# Revit family: PLC_ARR_3S
name_source: partatom
category: Mechanical Equipment
units: mm (PartAtom-declared; Revit-internal decimal feet)

## family parameters
Always vertical = Yes
Cut with Voids When Loaded = No
Part Type = Normal
Room Calculation Point = No
Round Connector Dimension = Use Diameter
Shared = No
Work Plane-Based = No

## types (40) — shared parameters
0 = 0' - 0"
1" = 0' - 1"
1.5 = 0' - 1 1/2"
120 = 90.00°
2" = 0' - 2"
2' = 2' - 0"
25 = 25.00°
3" = 0' - 3"
4" = 0' - 4"
60 = 60.00°
Manufacturer = Loren Cook Company
Model = PLC Arrangement 3S
ONE EIGTH = 0' - 0 1/8"
URL = www.lorencook.com

## per-type parameters (varying)
- 120_PLC_CLASS_1_3S: -(H-.125")=-0' - 1 11/16"; -F=-1' - 1 1/16"; -F/2=-0' - 6 17/32"; -H+.375"=-0' - 1 7/16"; A=1' - 5 1/4"; A/2=0' - 8 5/8"; B=1' - 5 1/4"; B/2=0' - 8 5/8"; C=0' - 8 5/8"; C*.2=0' - 2 19/32"; C*.66=0' - 5 11/16"; C-M=0' - 7 7/16"; C/2=0' - 4 5/16"; D=0' - 8 5/8"; E=0' - 7 11/16"; F=1' - 1 1/16"; F-H-H=0' - 9 7/16"; G=0' - 7 7/16"; H=0' - 1 13/16"; H-.125"=0' - 1 11/16"; J=0' - 2 13/16"; K=1' - 4 15/16"; K-F=0' - 3 7/8"; L=0' - 0 5/8"; L/2=0' - 0 5/16"; M=0' - 1 3/16"; M*2=0' - 2 3/8"; M/2=0' - 0 19/32"; MB/2=0' - 5 1/4"; MH/2=0' - 5 1/4"; MOTOR_BASE=0' - 10 1/2"; MOTOR_HEIGHT=0' - 10 1/2"; N=1' - 4 3/4"; P=0' - 0 5/8"; Type Comments=Centrifugal Plenum Fan Side Mount Arrangement 3S Class 1
- 135_PLC_CLASS_1_3S: -(H-.125")=-0' - 1 15/16"; -F=-1' - 2 5/8"; -F/2=-0' - 7 5/16"; -H+.375"=-0' - 1 11/16"; A=1' - 7 1/2"; A/2=0' - 9 3/4"; B=1' - 7 1/2"; B/2=0' - 9 3/4"; C=0' - 9 3/4"; C*.2=0' - 2 15/16"; C*.66=0' - 6 7/16"; C-M=0' - 8 9/16"; C/2=0' - 4 7/8"; D=0' - 9 3/4"; E=0' - 8 13/16"; F=1' - 2 5/8"; F-H-H=0' - 10 1/2"; G=0' - 8 1/2"; H=0' - 2 1/16"; H-.125"=0' - 1 15/16"; J=0' - 3 1/16"; K=1' - 6 1/2"; K-F=0' - 3 7/8"; L=0' - 0 5/8"; L/2=0' - 0 5/16"; M=0' - 1 3/16"; M*2=0' - 2 3/8"; M/2=0' - 0 19/32"; MB/2=0' - 5 1/4"; MH/2=0' - 5 1/4"; MOTOR_BASE=0' - 10 1/2"; MOTOR_HEIGHT=0' - 10 1/2"; N=1' - 6 5/8"; P=0' - 0 5/8"; Type Comments=Centrifugal Plenum Fan Side Mount Arrangement 3S Class 1
- 150_PLC_CLASS_1_3S: -(H-.125")=-0' - 1 15/16"; -F=-1' - 3 9/16"; -F/2=-0' - 7 25/32"; -H+.375"=-0' - 1 11/16"; A=1' - 9 1/2"; A/2=0' - 10 3/4"; B=1' - 9 1/2"; B/2=0' - 10 3/4"; C=0' - 10 3/4"; C*.2=0' - 3 7/32"; C*.66=0' - 7 3/32"; C-M=0' - 9 9/16"; C/2=0' - 5 3/8"; D=0' - 10 3/4"; E=0' - 9 13/16"; F=1' - 3 9/16"; F-H-H=0' - 11 7/16"; G=0' - 9 7/16"; H=0' - 2 1/16"; H-.125"=0' - 1 15/16"; J=0' - 3 1/16"; K=1' - 7 7/16"; K-F=0' - 3 7/8"; L=0' - 0 5/8"; L/2=0' - 0 5/16"; M=0' - 1 3/16"; M*2=0' - 2 3/8"; M/2=0' - 0 19/32"; MB/2=0' - 5 1/4"; MH/2=0' - 5 1/4"; MOTOR_BASE=0' - 10 1/2"; MOTOR_HEIGHT=0' - 10 1/2"; N=1' - 8 1/8"; P=0' - 0 5/8"; Type Comments=Centrifugal Plenum Fan Side Mount Arrangement 3S Class 1
- 165_PLC_CLASS_1_3S: -(H-.125")=-0' - 1 15/16"; -F=-1' - 4 3/4"; -F/2=-0' - 8 3/8"; -H+.375"=-0' - 1 11/16"; A=1' - 11 3/4"; A/2=0' - 11 7/8"; B=1' - 11 3/4"; B/2=0' - 11 7/8"; C=0' - 11 7/8"; C*.2=0' - 3 9/16"; C*.66=0' - 7 27/32"; C-M=0' - 10 11/16"; C/2=0' - 5 15/16"; D=0' - 11 7/8"; E=0' - 10 15/16"; F=1' - 4 3/4"; F-H-H=1' - 0 5/8"; G=0' - 10 5/8"; H=0' - 2 1/16"; H-.125"=0' - 1 15/16"; J=0' - 3 1/16"; K=1' - 8 5/8"; K-F=0' - 3 7/8"; L=0' - 0 5/8"; L/2=0' - 0 5/16"; M=0' - 1 3/16"; M*2=0' - 2 3/8"; M/2=0' - 0 19/32"; MB/2=0' - 5 1/4"; MH/2=0' - 5 1/4"; MOTOR_BASE=0' - 10 1/2"; MOTOR_HEIGHT=0' - 10 1/2"; N=1' - 9 3/4"; P=0' - 0 5/8"; Type Comments=Centrifugal Plenum Fan Side Mount Arrangement 3S Class 1
- 180_PLC_CLASS_1_3S: -(H-.125")=-0' - 2 15/16"; -F=-1' - 7 7/8"; -F/2=-0' - 9 15/16"; -H+.375"=-0' - 2 11/16"; A=2' - 1 3/4"; A/2=1' - 0 7/8"; B=2' - 1 3/4"; B/2=1' - 0 7/8"; C=1' - 0 7/8"; C*.2=0' - 3 7/8"; C*.66=0' - 8 1/2"; C-M=0' - 11 7/16"; C/2=0' - 6 7/16"; D=1' - 0 7/8"; E=1' - 0"; F=1' - 7 7/8"; F-H-H=1' - 1 3/4"; G=0' - 11 3/4"; H=0' - 3 1/16"; H-.125"=0' - 2 15/16"; J=0' - 4 1/16"; K=2' - 0"; K-F=0' - 4 1/8"; L=0' - 0 5/8"; L/2=0' - 0 5/16"; M=0' - 1 7/16"; M*2=0' - 2 7/8"; M/2=0' - 0 23/32"; MB/2=0' - 5 1/4"; MH/2=0' - 5 1/4"; MOTOR_BASE=0' - 10 1/2"; MOTOR_HEIGHT=0' - 10 1/2"; N=1' - 11 1/4"; P=0' - 0 5/8"; Type Comments=Centrifugal Plenum Fan Side Mount Arrangement 3S Class 1
- 195_PLC_CLASS_1_3S: -(H-.125")=-0' - 2 15/16"; -F=-1' - 9"; -F/2=-0' - 10 1/2"; -H+.375"=-0' - 2 11/16"; A=2' - 4"; A/2=1' - 2"; B=2' - 4"; B/2=1' - 2"; C=1' - 2"; C*.2=0' - 4 3/16"; C*.66=0' - 9 1/4"; C-M=1' - 0 9/16"; C/2=0' - 7"; D=1' - 2"; E=1' - 1 1/8"; F=1' - 9"; F-H-H=1' - 2 7/8"; G=1' - 0 7/8"; H=0' - 3 1/16"; H-.125"=0' - 2 15/16"; J=0' - 4 1/16"; K=2' - 1 1/8"; K-F=0' - 4 1/8"; L=0' - 0 5/8"; L/2=0' - 0 5/16"; M=0' - 1 7/16"; M*2=0' - 2 7/8"; M/2=0' - 0 23/32"; MB/2=0' - 6 5/16"; MH/2=0' - 6 5/16"; MOTOR_BASE=1' - 0 5/8"; MOTOR_HEIGHT=1' - 0 5/8"; N=2' - 1"; P=0' - 0 5/8"; Type Comments=Centrifugal Plenum Fan Side Mount Arrangement 3S Class 1
- 210_PLC_CLASS_1_3S: -(H-.125")=-0' - 2 15/16"; -F=-1' - 10 1/16"; -F/2=-0' - 11 1/32"; -H+.375"=-0' - 2 11/16"; A=2' - 6"; A/2=1' - 3"; B=2' - 6"; B/2=1' - 3"; C=1' - 3"; C*.2=0' - 4 1/2"; C*.66=0' - 9 29/32"; C-M=1' - 1 9/16"; C/2=0' - 7 1/2"; D=1' - 3"; E=1' - 2 1/8"; F=1' - 10 1/16"; F-H-H=1' - 3 15/16"; G=1' - 1 15/16"; H=0' - 3 1/16"; H-.125"=0' - 2 15/16"; J=0' - 4 1/16"; K=2' - 2 3/16"; K-F=0' - 4 1/8"; L=0' - 0 5/8"; L/2=0' - 0 5/16"; M=0' - 1 7/16"; M*2=0' - 2 7/8"; M/2=0' - 0 23/32"; MB/2=0' - 6 5/16"; MH/2=0' - 6 5/16"; MOTOR_BASE=1' - 0 5/8"; MOTOR_HEIGHT=1' - 0 5/8"; N=2' - 2 1/2"; P=0' - 1"; Type Comments=Centrifugal Plenum Fan Side Mount Arrangement 3S Class 1
- 225_PLC_CLASS_1_3S: -(H-.125")=-0' - 2 15/16"; -F=-1' - 11 1/16"; -F/2=-0' - 11 17/32"; -H+.375"=-0' - 2 11/16"; A=2' - 8 1/4"; A/2=1' - 4 1/8"; B=2' - 8 1/4"; B/2=1' - 4 1/8"; C=1' - 4 1/8"; C*.2=0' - 4 27/32"; C*.66=0' - 10 21/32"; C-M=1' - 2 11/16"; C/2=0' - 8 1/16"; D=1' - 4 1/8"; E=1' - 3 5/16"; F=1' - 11 1/16"; F-H-H=1' - 4 15/16"; G=1' - 2 15/16"; H=0' - 3 1/16"; H-.125"=0' - 2 15/16"; J=0' - 4 1/16"; K=2' - 3 3/16"; K-F=0' - 4 1/8"; L=0' - 0 5/8"; L/2=0' - 0 5/16"; M=0' - 1 7/16"; M*2=0' - 2 7/8"; M/2=0' - 0 23/32"; MB/2=0' - 6 5/16"; MH/2=0' - 6 5/16"; MOTOR_BASE=1' - 0 5/8"; MOTOR_HEIGHT=1' - 0 5/8"; N=2' - 4 1/8"; P=0' - 1"; Type Comments=Centrifugal Plenum Fan Side Mount Arrangement 3S Class 1
- 245_PLC_CLASS_1_3S: -(H-.125")=-0' - 2 15/16"; -F=-2' - 0 1/2"; -F/2=-1' - 0 1/4"; -H+.375"=-0' - 2 11/16"; A=2' - 11"; A/2=1' - 5 1/2"; B=2' - 11"; B/2=1' - 5 1/2"; C=1' - 5 1/2"; C*.2=0' - 5 1/4"; C*.66=0' - 11 9/16"; C-M=1' - 4 1/16"; C/2=0' - 8 3/4"; D=1' - 5 1/2"; E=1' - 4 7/16"; F=2' - 0 1/2"; F-H-H=1' - 6 3/8"; G=1' - 3 7/8"; H=0' - 3 1/16"; H-.125"=0' - 2 15/16"; J=0' - 4 5/16"; K=2' - 4 3/4"; K-F=0' - 4 1/4"; L=0' - 0 5/8"; L/2=0' - 0 5/16"; M=0' - 1 7/16"; M*2=0' - 2 7/8"; M/2=0' - 0 23/32"; MB/2=0' - 6 5/16"; MH/2=0' - 6 5/16"; MOTOR_BASE=1' - 0 5/8"; MOTOR_HEIGHT=1' - 0 5/8"; N=2' - 6 1/8"; P=0' - 1"; Type Comments=Centrifugal Plenum Fan Side Mount Arrangement 3S Class 1
- 270_PLC_CLASS_1_3S: -(H-.125")=-0' - 3 7/16"; -F=-2' - 3 7/16"; -F/2=-1' - 1 23/32"; -H+.375"=-0' - 3 3/16"; A=3' - 2 3/4"; A/2=1' - 7 3/8"; B=3' - 2 3/4"; B/2=1' - 7 3/8"; C=1' - 7 3/8"; C*.2=0' - 5 13/16"; C*.66=1' - 0 25/32"; C-M=1' - 5 15/16"; C/2=0' - 9 11/16"; D=1' - 7 3/8"; E=1' - 6 5/16"; F=2' - 3 7/16"; F-H-H=1' - 8 5/16"; G=1' - 5 13/16"; H=0' - 3 9/16"; H-.125"=0' - 3 7/16"; J=0' - 4 13/16"; K=2' - 7 11/16"; K-F=0' - 4 1/4"; L=0' - 0 5/8"; L/2=0' - 0 5/16"; M=0' - 1 7/16"; M*2=0' - 2 7/8"; M/2=0' - 0 23/32"; MB/2=0' - 7"; MH/2=0' - 7"; MOTOR_BASE=1' - 2"; MOTOR_HEIGHT=1' - 2"; N=2' - 10 1/2"; P=0' - 1"; Type Comments=Centrifugal Plenum Fan Side Mount Arrangement 3S Class 1
- 300_PLC_CLASS_1_3S: -(H-.125")=-0' - 3 7/16"; -F=-2' - 5 1/2"; -F/2=-1' - 2 3/4"; -H+.375"=-0' - 3 3/16"; A=3' - 7"; A/2=1' - 9 1/2"; B=3' - 7"; B/2=1' - 9 1/2"; C=1' - 9 1/2"; C*.2=0' - 6 7/16"; C*.66=1' - 2 3/16"; C-M=1' - 7 13/16"; C/2=0' - 10 3/4"; D=1' - 9 1/2"; E=1' - 8 3/16"; F=2' - 5 1/2"; F-H-H=1' - 10 3/8"; G=1' - 7 3/8"; H=0' - 3 9/16"; H-.125"=0' - 3 7/16"; J=0' - 5 1/16"; K=2' - 9 7/8"; K-F=0' - 4 3/8"; L=0' - 0 5/8"; L/2=0' - 0 5/16"; M=0' - 1 11/16"; M*2=0' - 3 3/8"; M/2=0' - 0 27/32"; MB/2=0' - 7"; MH/2=0' - 7"; MOTOR_BASE=1' - 2"; MOTOR_HEIGHT=1' - 2"; N=2' - 11 5/8"; P=0' - 1"; Type Comments=Centrifugal Plenum Fan Side Mount Arrangement 3S Class 1
- 330_PLC_CLASS_1_3S: -(H-.125")=-0' - 3 7/16"; -F=-2' - 8 3/16"; -F/2=-1' - 4 3/32"; -H+.375"=-0' - 3 3/16"; A=4' - 1 1/2"; A/2=2' - 0 3/4"; B=3' - 10"; B/2=1' - 11"; C=1' - 11 5/8"; C*.2=0' - 7 3/32"; C*.66=1' - 3 19/32"; C-M=1' - 9 11/16"; C/2=0' - 11 13/16"; D=1' - 11"; E=1' - 10 5/16"; F=2' - 8 3/16"; F-H-H=2' - 1 1/16"; G=2' - 2 3/8"; H=0' - 3 9/16"; H-.125"=0' - 3 7/16"; J=0' - 4 11/16"; K=3' - 0 13/16"; K-F=0' - 4 5/8"; L=0' - 0 15/16"; L/2=0' - 0 15/32"; M=0' - 1 15/16"; M*2=0' - 3 7/8"; M/2=0' - 0 31/32"; MB/2=0' - 6 5/16"; MH/2=0' - 6 5/16"; MOTOR_BASE=1' - 0 5/8"; MOTOR_HEIGHT=1' - 0 5/8"; N=3' - 1 5/8"; P=0' - 1"; Type Comments=Centrifugal Plenum Fan Side Mount Arrangement 3S Class 1
- 365_PLC_CLASS_1_3S: -(H-.125")=-0' - 3 7/16"; -F=-2' - 10 9/16"; -F/2=-1' - 5 9/32"; -H+.375"=-0' - 3 3/16"; A=4' - 5 1/2"; A/2=2' - 2 3/4"; B=4' - 1"; B/2=2' - 0 1/2"; C=2' - 2 1/8"; C*.2=0' - 7 27/32"; C*.66=1' - 5 1/4"; C-M=2' - 0 3/16"; C/2=1' - 1 1/16"; D=2' - 0 1/2"; E=1' - 11 13/16"; F=2' - 10 9/16"; F-H-H=2' - 3 7/16"; G=2' - 4 3/4"; H=0' - 3 9/16"; H-.125"=0' - 3 7/16"; J=0' - 4 11/16"; K=3' - 3 5/16"; K-F=0' - 4 3/4"; L=0' - 0 15/16"; L/2=0' - 0 15/32"; M=0' - 1 15/16"; M*2=0' - 3 7/8"; M/2=0' - 0 31/32"; MB/2=0' - 6 5/16"; MH/2=0' - 6 5/16"; MOTOR_BASE=1' - 0 5/8"; MOTOR_HEIGHT=1' - 0 5/8"; N=3' - 4"; P=0' - 1"; Type Comments=Centrifugal Plenum Fan Side Mount Arrangement 3S Class 1
- 402_PLC_CLASS_1_3S: -(H-.125")=-0' - 4 7/16"; -F=-3' - 3 7/16"; -F/2=-1' - 7 23/32"; -H+.375"=-0' - 4 3/16"; A=5' - 0"; A/2=2' - 6"; B=4' - 6"; B/2=2' - 3"; C=2' - 4 3/4"; C*.2=0' - 8 5/8"; C*.66=1' - 6 31/32"; C-M=2' - 2 5/16"; C/2=1' - 2 3/8"; D=2' - 3"; E=2' - 2 1/4"; F=3' - 3 7/16"; F-H-H=2' - 6 5/16"; G=2' - 8 5/8"; H=0' - 4 9/16"; H-.125"=0' - 4 7/16"; J=0' - 5 11/16"; K=3' - 8 7/16"; K-F=0' - 5"; L=0' - 0 15/16"; L/2=0' - 0 15/32"; M=0' - 2 7/16"; M*2=0' - 4 7/8"; M/2=0' - 1 7/32"; MB/2=0' - 7"; MH/2=0' - 7"; MOTOR_BASE=1' - 2"; MOTOR_HEIGHT=1' - 2"; N=3' - 7 7/8"; P=0' - 1"; Type Comments=Centrifugal Plenum Fan Side Mount Arrangement 3S Class 1
- 445_PLC_CLASS_1_3S: -(H-.125")=-0' - 4 15/16"; -F=-3' - 7"; -F/2=-1' - 9 1/2"; -H+.375"=-0' - 4 11/16"; A=5' - 4"; A/2=2' - 8"; B=4' - 10 1/2"; B/2=2' - 5 1/4"; C=2' - 7 7/8"; C*.2=0' - 9 9/16"; C*.66=1' - 9 1/32"; C-M=2' - 5 7/16"; C/2=1' - 3 15/16"; D=2' - 5 1/4"; E=2' - 4 1/2"; F=3' - 7"; F-H-H=2' - 8 7/8"; G=2' - 11 5/8"; H=0' - 5 1/16"; H-.125"=0' - 4 15/16"; J=0' - 6 1/4"; K=4' - 0 1/8"; K-F=0' - 5 1/8"; L=0' - 0 15/16"; L/2=0' - 0 15/32"; M=0' - 2 7/16"; M*2=0' - 4 7/8"; M/2=0' - 1 7/32"; MB/2=0' - 8"; MH/2=0' - 8"; MOTOR_BASE=1' - 4"; MOTOR_HEIGHT=1' - 4"; N=3' - 11 1/8"; P=0' - 1"; Type Comments=Centrifugal Plenum Fan Side Mount Arrangement 3S Class 1
- 490_PLC_CLASS_1_3S: -(H-.125")=-0' - 4 15/16"; -F=-3' - 11 1/4"; -F/2=-1' - 11 5/8"; -H+.375"=-0' - 4 11/16"; A=5' - 10"; A/2=2' - 11"; B=5' - 3"; B/2=2' - 7 1/2"; C=2' - 11"; C*.2=0' - 10 1/2"; C*.66=1' - 11 3/32"; C-M=2' - 8 9/16"; C/2=1' - 5 1/2"; D=2' - 7 1/2"; E=2' - 6 5/8"; F=3' - 11 1/4"; F-H-H=3' - 1 1/8"; G=3' - 3 7/8"; H=0' - 5 1/16"; H-.125"=0' - 4 15/16"; J=0' - 6 1/4"; K=4' - 4 5/8"; K-F=0' - 5 3/8"; L=0' - 0 15/16"; L/2=0' - 0 15/32"; M=0' - 2 7/16"; M*2=0' - 4 7/8"; M/2=0' - 1 7/32"; MB/2=0' - 8"; MH/2=0' - 8"; MOTOR_BASE=1' - 4"; MOTOR_HEIGHT=1' - 4"; N=4' - 2 3/8"; P=0' - 1"; Type Comments=Centrifugal Plenum Fan Side Mount Arrangement 3S Class 1
- 540_PLC_CLASS_1_3S: -(H-.125")=-0' - 5"; -F=-4' - 2 7/8"; -F/2=-2' - 1 7/16"; -H+.375"=-0' - 4 3/4"; A=6' - 3"; A/2=3' - 1 1/2"; B=5' - 9"; B/2=2' - 10 1/2"; C=3' - 2 5/8"; C*.2=0' - 11 19/32"; C*.66=2' - 1 1/2"; C-M=3' - 0 3/16"; C/2=1' - 7 5/16"; D=2' - 10 1/2"; E=2' - 9 5/8"; F=4' - 2 7/8"; F-H-H=3' - 4 5/8"; G=3' - 7 1/2"; H=0' - 5 1/8"; H-.125"=0' - 5"; J=0' - 6 1/4"; K=4' - 8 1/2"; K-F=0' - 5 5/8"; L=0' - 1 1/16"; L/2=0' - 0 17/32"; M=0' - 2 7/16"; M*2=0' - 4 7/8"; M/2=0' - 1 7/32"; MB/2=0' - 8"; MH/2=0' - 8"; MOTOR_BASE=1' - 4"; MOTOR_HEIGHT=1' - 4"; N=4' - 6 1/4"; P=0' - 1 1/4"; Type Comments=Centrifugal Plenum Fan Side Mount Arrangement 3S Class 1
- 600_PLC_CLASS_1_3S: -(H-.125")=-0' - 6"; -F=-4' - 10 1/4"; -F/2=-2' - 5 1/8"; -H+.375"=-0' - 5 3/4"; A=6' - 10"; A/2=3' - 5"; B=6' - 3"; B/2=3' - 1 1/2"; C=3' - 6 7/8"; C*.2=1' - 0 7/8"; C*.66=2' - 4 5/16"; C-M=3' - 4 3/16"; C/2=1' - 9 7/16"; D=3' - 1 1/2"; E=3' - 0 5/8"; F=4' - 10 1/4"; F-H-H=3' - 10"; G=3' - 11 7/8"; H=0' - 6 1/8"; H-.125"=0' - 6"; J=0' - 7 1/4"; K=5' - 2 1/4"; K-F=0' - 4"; L=0' - 1 1/16"; L/2=0' - 0 17/32"; M=0' - 2 11/16"; M*2=0' - 5 3/8"; M/2=0' - 1 11/32"; MB/2=0' - 9"; MH/2=0' - 9"; MOTOR_BASE=1' - 6"; MOTOR_HEIGHT=1' - 6"; N=4' - 9 7/8"; P=0' - 1 1/4"; Type Comments=Centrifugal Plenum Fan Side Mount Arrangement 3S Class 1
- 660_PLC_CLASS_1_3S: -(H-.125")=-0' - 7"; -F=-5' - 3 11/16"; -F/2=-2' - 7 27/32"; -H+.375"=-0' - 6 3/4"; A=7' - 6"; A/2=3' - 9"; B=6' - 10"; B/2=3' - 5"; C=3' - 11 1/4"; C*.2=1' - 2 3/16"; C*.66=2' - 7 3/16"; C-M=3' - 8 5/16"; C/2=1' - 11 5/8"; D=3' - 5"; E=3' - 4"; F=5' - 3 11/16"; F-H-H=4' - 1 7/16"; G=4' - 6 5/16"; H=0' - 7 1/8"; H-.125"=0' - 7"; J=0' - 8 1/4"; K=5' - 10 5/16"; K-F=0' - 6 5/8"; L=0' - 1 1/16"; L/2=0' - 0 17/32"; M=0' - 2 15/16"; M*2=0' - 5 7/8"; M/2=0' - 1 15/32"; MB/2=0' - 9"; MH/2=0' - 9"; MOTOR_BASE=1' - 6"; MOTOR_HEIGHT=1' - 6"; N=5' - 2 7/8"; P=0' - 1 1/2"; Type Comments=Centrifugal Plenum Fan Side Mount Arrangement 3S Class 1
- 730_PLC_CLASS_1_3S: -(H-.125")=-0' - 8"; -F=-5' - 9 11/16"; -F/2=-2' - 10 27/32"; -H+.375"=-0' - 7 3/4"; A=7' - 8"; A/2=3' - 10"; B=7' - 8"; B/2=3' - 10"; C=4' - 4 1/4"; C*.2=1' - 3 11/16"; C*.66=2' - 10 1/2"; C-M=4' - 0 13/16"; C/2=2' - 2 1/8"; D=3' - 10"; E=3' - 9"; F=5' - 9 11/16"; F-H-H=4' - 5 7/16"; G=4' - 11 5/16"; H=0' - 8 1/8"; H-.125"=0' - 8"; J=0' - 9 1/4"; K=6' - 4 15/16"; K-F=0' - 7 1/4"; L=0' - 1 1/16"; L/2=0' - 0 17/32"; M=0' - 3 7/16"; M*2=0' - 6 7/8"; M/2=0' - 1 23/32"; MB/2=0' - 11"; MH/2=0' - 11 3/4"; MOTOR_BASE=1' - 10"; MOTOR_HEIGHT=1' - 11 1/2"; N=5' - 8 1/2"; P=0' - 1 1/2"; Type Comments=Centrifugal Plenum Fan Side Mount Arrangement 3S Class 1
- 120_PLC_CLASS_2_3S: -(H-.125")=-0' - 1 11/16"; -F=-1' - 1 1/16"; -F/2=-0' - 6 17/32"; -H+.375"=-0' - 1 7/16"; A=1' - 5 1/4"; A/2=0' - 8 5/8"; B=1' - 5 1/4"; B/2=0' - 8 5/8"; C=0' - 8 5/8"; C*.2=0' - 2 19/32"; C*.66=0' - 5 11/16"; C-M=0' - 7 3/16"; C/2=0' - 4 5/16"; D=0' - 8 5/8"; E=0' - 7 11/16"; F=1' - 1 1/16"; F-H-H=0' - 9 7/16"; G=0' - 7 7/16"; H=0' - 1 13/16"; H-.125"=0' - 1 11/16"; J=0' - 2 13/16"; K=1' - 5 5/16"; K-F=0' - 4 1/4"; L=0' - 0 5/8"; L/2=0' - 0 5/16"; M=0' - 1 7/16"; M*2=0' - 2 7/8"; M/2=0' - 0 23/32"; MB/2=0' - 5 1/4"; MH/2=0' - 5 1/4"; MOTOR_BASE=0' - 10 1/2"; MOTOR_HEIGHT=0' - 10 1/2"; N=1' - 4 3/4"; P=0' - 0 5/8"; Type Comments=Centrifugal Plenum Fan Side Mount Arrangement 3S Class 2
- 135_PLC_CLASS_2_3S: -(H-.125")=-0' - 1 15/16"; -F=-1' - 2 5/8"; -F/2=-0' - 7 5/16"; -H+.375"=-0' - 1 11/16"; A=1' - 7 1/2"; A/2=0' - 9 3/4"; B=1' - 7 1/2"; B/2=0' - 9 3/4"; C=0' - 9 3/4"; C*.2=0' - 2 15/16"; C*.66=0' - 6 7/16"; C-M=0' - 8 5/16"; C/2=0' - 4 7/8"; D=0' - 9 3/4"; E=0' - 8 13/16"; F=1' - 2 5/8"; F-H-H=0' - 10 1/2"; G=0' - 8 1/2"; H=0' - 2 1/16"; H-.125"=0' - 1 15/16"; J=0' - 3 1/16"; K=1' - 6 7/8"; K-F=0' - 4 1/4"; L=0' - 0 5/8"; L/2=0' - 0 5/16"; M=0' - 1 7/16"; M*2=0' - 2 7/8"; M/2=0' - 0 23/32"; MB/2=0' - 5 1/4"; MH/2=0' - 5 1/4"; MOTOR_BASE=0' - 10 1/2"; MOTOR_HEIGHT=0' - 10 1/2"; N=1' - 6 5/8"; P=0' - 0 5/8"; Type Comments=Centrifugal Plenum Fan Side Mount Arrangement 3S Class 2
- 150_PLC_CLASS_2_3S: -(H-.125")=-0' - 1 15/16"; -F=-1' - 3 9/16"; -F/2=-0' - 7 25/32"; -H+.375"=-0' - 1 11/16"; A=1' - 9 1/2"; A/2=0' - 10 3/4"; B=1' - 9 1/2"; B/2=0' - 10 3/4"; C=0' - 10 3/4"; C*.2=0' - 3 7/32"; C*.66=0' - 7 3/32"; C-M=0' - 9 5/16"; C/2=0' - 5 3/8"; D=0' - 10 3/4"; E=0' - 9 13/16"; F=1' - 3 9/16"; F-H-H=0' - 11 7/16"; G=0' - 9 7/16"; H=0' - 2 1/16"; H-.125"=0' - 1 15/16"; J=0' - 3 1/16"; K=1' - 7 13/16"; K-F=0' - 4 1/4"; L=0' - 0 5/8"; L/2=0' - 0 5/16"; M=0' - 1 7/16"; M*2=0' - 2 7/8"; M/2=0' - 0 23/32"; MB/2=0' - 5 1/4"; MH/2=0' - 5 1/4"; MOTOR_BASE=0' - 10 1/2"; MOTOR_HEIGHT=0' - 10 1/2"; N=1' - 8 1/8"; P=0' - 0 5/8"; Type Comments=Centrifugal Plenum Fan Side Mount Arrangement 3S Class 2
- 165_PLC_CLASS_2_3S: -(H-.125")=-0' - 1 15/16"; -F=-1' - 4 3/4"; -F/2=-0' - 8 3/8"; -H+.375"=-0' - 1 11/16"; A=1' - 11 3/4"; A/2=0' - 11 7/8"; B=1' - 11 3/4"; B/2=0' - 11 7/8"; C=0' - 11 7/8"; C*.2=0' - 3 9/16"; C*.66=0' - 7 27/32"; C-M=0' - 10 7/16"; C/2=0' - 5 15/16"; D=0' - 11 7/8"; E=0' - 10 15/16"; F=1' - 4 3/4"; F-H-H=1' - 0 5/8"; G=0' - 10 5/8"; H=0' - 2 1/16"; H-.125"=0' - 1 15/16"; J=0' - 3 1/16"; K=1' - 9"; K-F=0' - 4 1/4"; L=0' - 0 5/8"; L/2=0' - 0 5/16"; M=0' - 1 7/16"; M*2=0' - 2 7/8"; M/2=0' - 0 23/32"; MB/2=0' - 5 1/4"; MH/2=0' - 5 1/4"; MOTOR_BASE=0' - 10 1/2"; MOTOR_HEIGHT=0' - 10 1/2"; N=1' - 9 3/4"; P=0' - 0 5/8"; Type Comments=Centrifugal Plenum Fan Side Mount Arrangement 3S Class 2
- 180_PLC_CLASS_2_3S: -(H-.125")=-0' - 2 15/16"; -F=-1' - 7 7/8"; -F/2=-0' - 9 15/16"; -H+.375"=-0' - 2 11/16"; A=2' - 1 3/4"; A/2=1' - 0 7/8"; B=2' - 1 3/4"; B/2=1' - 0 7/8"; C=1' - 0 7/8"; C*.2=0' - 3 7/8"; C*.66=0' - 8 1/2"; C-M=0' - 11 7/16"; C/2=0' - 6 7/16"; D=1' - 0 7/8"; E=1' - 0"; F=1' - 7 7/8"; F-H-H=1' - 1 3/4"; G=0' - 11 3/4"; H=0' - 3 1/16"; H-.125"=0' - 2 15/16"; J=0' - 4 1/16"; K=2' - 0 1/8"; K-F=0' - 4 1/4"; L=0' - 0 5/8"; L/2=0' - 0 5/16"; M=0' - 1 7/16"; M*2=0' - 2 7/8"; M/2=0' - 0 23/32"; MB/2=0' - 5 1/4"; MH/2=0' - 5 1/4"; MOTOR_BASE=0' - 10 1/2"; MOTOR_HEIGHT=0' - 10 1/2"; N=1' - 11 1/4"; P=0' - 0 5/8"; Type Comments=Centrifugal Plenum Fan Side Mount Arrangement 3S Class 2
- 195_PLC_CLASS_2_3S: -(H-.125")=-0' - 2 15/16"; -F=-1' - 9"; -F/2=-0' - 10 1/2"; -H+.375"=-0' - 2 11/16"; A=2' - 4"; A/2=1' - 2"; B=2' - 4"; B/2=1' - 2"; C=1' - 2"; C*.2=0' - 4 3/16"; C*.66=0' - 9 1/4"; C-M=1' - 0 9/16"; C/2=0' - 7"; D=1' - 2"; E=1' - 1 1/8"; F=1' - 9"; F-H-H=1' - 2 7/8"; G=1' - 0 7/8"; H=0' - 3 1/16"; H-.125"=0' - 2 15/16"; J=0' - 4 1/16"; K=2' - 1 1/4"; K-F=0' - 4 1/4"; L=0' - 0 5/8"; L/2=0' - 0 5/16"; M=0' - 1 7/16"; M*2=0' - 2 7/8"; M/2=0' - 0 23/32"; MB/2=0' - 6 5/16"; MH/2=0' - 6 5/16"; MOTOR_BASE=1' - 0 5/8"; MOTOR_HEIGHT=1' - 0 5/8"; N=2' - 1"; P=0' - 0 5/8"; Type Comments=Centrifugal Plenum Fan Side Mount Arrangement 3S Class 2
- 210_PLC_CLASS_2_3S: -(H-.125")=-0' - 2 15/16"; -F=-1' - 10 1/16"; -F/2=-0' - 11 1/32"; -H+.375"=-0' - 2 11/16"; A=2' - 6"; A/2=1' - 3"; B=2' - 6"; B/2=1' - 3"; C=1' - 3"; C*.2=0' - 4 1/2"; C*.66=0' - 9 29/32"; C-M=1' - 1 9/16"; C/2=0' - 7 1/2"; D=1' - 3"; E=1' - 2 1/8"; F=1' - 10 1/16"; F-H-H=1' - 3 15/16"; G=1' - 1 15/16"; H=0' - 3 1/16"; H-.125"=0' - 2 15/16"; J=0' - 4 1/16"; K=2' - 2 7/16"; K-F=0' - 4 3/8"; L=0' - 0 5/8"; L/2=0' - 0 5/16"; M=0' - 1 7/16"; M*2=0' - 2 7/8"; M/2=0' - 0 23/32"; MB/2=0' - 6 5/16"; MH/2=0' - 6 5/16"; MOTOR_BASE=1' - 0 5/8"; MOTOR_HEIGHT=1' - 0 5/8"; N=2' - 2 1/2"; P=0' - 1"; Type Comments=Centrifugal Plenum Fan Side Mount Arrangement 3S Class 2
- 225_PLC_CLASS_2_3S: -(H-.125")=-0' - 2 15/16"; -F=-1' - 11 1/16"; -F/2=-0' - 11 17/32"; -H+.375"=-0' - 2 11/16"; A=2' - 8 1/4"; A/2=1' - 4 1/8"; B=2' - 8 1/4"; B/2=1' - 4 1/8"; C=1' - 4 1/8"; C*.2=0' - 4 27/32"; C*.66=0' - 10 21/32"; C-M=1' - 2 7/16"; C/2=0' - 8 1/16"; D=1' - 4 1/8"; E=1' - 3 5/16"; F=1' - 11 1/16"; F-H-H=1' - 4 15/16"; G=1' - 2 15/16"; H=0' - 3 1/16"; H-.125"=0' - 2 15/16"; J=0' - 4 1/16"; K=2' - 3 7/16"; K-F=0' - 4 3/8"; L=0' - 0 5/8"; L/2=0' - 0 5/16"; M=0' - 1 11/16"; M*2=0' - 3 3/8"; M/2=0' - 0 27/32"; MB/2=0' - 6 5/16"; MH/2=0' - 6 5/16"; MOTOR_BASE=1' - 0 5/8"; MOTOR_HEIGHT=1' - 0 5/8"; N=2' - 4 1/8"; P=0' - 1"; Type Comments=Centrifugal Plenum Fan Side Mount Arrangement 3S Class 2
- 245_PLC_CLASS_2_3S: -(H-.125")=-0' - 2 15/16"; -F=-2' - 0 1/2"; -F/2=-1' - 0 1/4"; -H+.375"=-0' - 2 11/16"; A=2' - 11"; A/2=1' - 5 1/2"; B=2' - 11"; B/2=1' - 5 1/2"; C=1' - 5 1/2"; C*.2=0' - 5 1/4"; C*.66=0' - 11 9/16"; C-M=1' - 3 9/16"; C/2=0' - 8 3/4"; D=1' - 5 1/2"; E=1' - 4 7/16"; F=2' - 0 1/2"; F-H-H=1' - 6 3/8"; G=1' - 3 7/8"; H=0' - 3 1/16"; H-.125"=0' - 2 15/16"; J=0' - 4 5/16"; K=2' - 5"; K-F=0' - 4 1/2"; L=0' - 0 5/8"; L/2=0' - 0 5/16"; M=0' - 1 15/16"; M*2=0' - 3 7/8"; M/2=0' - 0 31/32"; MB/2=0' - 6 5/16"; MH/2=0' - 6 5/16"; MOTOR_BASE=1' - 0 5/8"; MOTOR_HEIGHT=1' - 0 5/8"; N=2' - 6 1/8"; P=0' - 1"; Type Comments=Centrifugal Plenum Fan Side Mount Arrangement 3S Class 2
- 270_PLC_CLASS_2_3S: -(H-.125")=-0' - 3 7/16"; -F=-2' - 3 7/16"; -F/2=-1' - 1 23/32"; -H+.375"=-0' - 3 3/16"; A=3' - 2 3/4"; A/2=1' - 7 3/8"; B=3' - 2 3/4"; B/2=1' - 7 3/8"; C=1' - 7 3/8"; C*.2=0' - 5 13/16"; C*.66=1' - 0 25/32"; C-M=1' - 5 7/16"; C/2=0' - 9 11/16"; D=1' - 7 3/8"; E=1' - 6 5/16"; F=2' - 3 7/16"; F-H-H=1' - 8 5/16"; G=1' - 5 13/16"; H=0' - 3 9/16"; H-.125"=0' - 3 7/16"; J=0' - 4 13/16"; K=2' - 8 1/16"; K-F=0' - 4 5/8"; L=0' - 0 5/8"; L/2=0' - 0 5/16"; M=0' - 1 15/16"; M*2=0' - 3 7/8"; M/2=0' - 0 31/32"; MB/2=0' - 7"; MH/2=0' - 7"; MOTOR_BASE=1' - 2"; MOTOR_HEIGHT=1' - 2"; N=2' - 10 1/2"; P=0' - 1"; Type Comments=Centrifugal Plenum Fan Side Mount Arrangement 3S Class 2
- 300_PLC_CLASS_2_3S: -(H-.125")=-0' - 3 7/16"; -F=-2' - 5 1/2"; -F/2=-1' - 2 3/4"; -H+.375"=-0' - 3 3/16"; A=3' - 7"; A/2=1' - 9 1/2"; B=3' - 7"; B/2=1' - 9 1/2"; C=1' - 9 1/2"; C*.2=0' - 6 7/16"; C*.66=1' - 2 3/16"; C-M=1' - 7 5/16"; C/2=0' - 10 3/4"; D=1' - 9 1/2"; E=1' - 8 3/16"; F=2' - 5 1/2"; F-H-H=1' - 10 3/8"; G=1' - 7 3/8"; H=0' - 3 9/16"; H-.125"=0' - 3 7/16"; J=0' - 5 1/16"; K=2' - 10 1/4"; K-F=0' - 4 3/4"; L=0' - 0 5/8"; L/2=0' - 0 5/16"; M=0' - 2 3/16"; M*2=0' - 4 3/8"; M/2=0' - 1 3/32"; MB/2=0' - 7"; MH/2=0' - 7"; MOTOR_BASE=1' - 2"; MOTOR_HEIGHT=1' - 2"; N=2' - 11 5/8"; P=0' - 1"; Type Comments=Centrifugal Plenum Fan Side Mount Arrangement 3S Class 2
- 330_PLC_CLASS_2_3S: -(H-.125")=-0' - 4 7/16"; -F=-2' - 10 3/16"; -F/2=-1' - 5 3/32"; -H+.375"=-0' - 4 3/16"; A=4' - 1 1/2"; A/2=2' - 0 3/4"; B=3' - 10"; B/2=1' - 11"; C=1' - 11 5/8"; C*.2=0' - 7 3/32"; C*.66=1' - 3 19/32"; C-M=1' - 9 7/16"; C/2=0' - 11 13/16"; D=1' - 11"; E=1' - 10 1/4"; F=2' - 10 3/16"; F-H-H=2' - 1 1/16"; G=2' - 3 3/8"; H=0' - 4 9/16"; H-.125"=0' - 4 7/16"; J=0' - 5 11/16"; K=3' - 3 1/16"; K-F=0' - 4 7/8"; L=0' - 0 15/16"; L/2=0' - 0 15/32"; M=0' - 2 3/16"; M*2=0' - 4 3/8"; M/2=0' - 1 3/32"; MB/2=0' - 8"; MH/2=0' - 8"; MOTOR_BASE=1' - 4"; MOTOR_HEIGHT=1' - 4"; N=3' - 1 5/8"; P=0' - 1"; Type Comments=Centrifugal Plenum Fan Side Mount Arrangement 3S Class 2
- 365_PLC_CLASS_2_3S: -(H-.125")=-0' - 4 7/16"; -F=-3' - 0 5/8"; -F/2=-1' - 6 5/16"; -H+.375"=-0' - 4 3/16"; A=4' - 5 1/2"; A/2=2' - 2 3/4"; B=4' - 1"; B/2=2' - 0 1/2"; C=2' - 2 1/8"; C*.2=0' - 7 27/32"; C*.66=1' - 5 1/4"; C-M=1' - 11 15/16"; C/2=1' - 1 1/16"; D=2' - 0 1/2"; E=1' - 11 3/4"; F=3' - 0 5/8"; F-H-H=2' - 3 1/2"; G=2' - 5 13/16"; H=0' - 4 9/16"; H-.125"=0' - 4 7/16"; J=0' - 5 11/16"; K=3' - 5 5/8"; K-F=0' - 5"; L=0' - 0 15/16"; L/2=0' - 0 15/32"; M=0' - 2 3/16"; M*2=0' - 4 3/8"; M/2=0' - 1 3/32"; MB/2=0' - 8"; MH/2=0' - 8"; MOTOR_BASE=1' - 4"; MOTOR_HEIGHT=1' - 4"; N=3' - 4"; P=0' - 1"; Type Comments=Centrifugal Plenum Fan Side Mount Arrangement 3S Class 2
- 402_PLC_CLASS_2_3S: -(H-.125")=-0' - 4 15/16"; -F=-3' - 4 15/16"; -F/2=-1' - 8 15/32"; -H+.375"=-0' - 4 11/16"; A=5' - 0"; A/2=2' - 6"; B=4' - 6"; B/2=2' - 3"; C=2' - 4 3/4"; C*.2=0' - 8 5/8"; C*.66=1' - 6 31/32"; C-M=2' - 2 5/16"; C/2=1' - 2 3/8"; D=2' - 3"; E=2' - 2 1/8"; F=3' - 4 15/16"; F-H-H=2' - 6 13/16"; G=2' - 9 5/8"; H=0' - 5 1/16"; H-.125"=0' - 4 15/16"; J=0' - 5 11/16"; K=3' - 8 7/16"; K-F=0' - 3 1/2"; L=0' - 0 15/16"; L/2=0' - 0 15/32"; M=0' - 2 7/16"; M*2=0' - 4 7/8"; M/2=0' - 1 7/32"; MB/2=0' - 8"; MH/2=0' - 8"; MOTOR_BASE=1' - 4"; MOTOR_HEIGHT=1' - 4"; N=3' - 7 7/8"; P=0' - 1"; Type Comments=Centrifugal Plenum Fan Side Mount Arrangement 3S Class 2
- 445_PLC_CLASS_2_3S: -(H-.125")=-0' - 5 15/16"; -F=-3' - 9"; -F/2=-1' - 10 1/2"; -H+.375"=-0' - 5 11/16"; A=5' - 4"; A/2=2' - 8"; B=4' - 10 1/2"; B/2=2' - 5 1/4"; C=2' - 7 7/8"; C*.2=0' - 9 9/16"; C*.66=1' - 9 1/32"; C-M=2' - 5 7/16"; C/2=1' - 3 15/16"; D=2' - 5 1/4"; E=2' - 4 3/8"; F=3' - 9"; F-H-H=2' - 8 7/8"; G=3' - 0 5/8"; H=0' - 6 1/16"; H-.125"=0' - 5 15/16"; J=0' - 7 1/4"; K=4' - 2 3/4"; K-F=0' - 5 3/4"; L=0' - 0 15/16"; L/2=0' - 0 15/32"; M=0' - 2 7/16"; M*2=0' - 4 7/8"; M/2=0' - 1 7/32"; MB/2=0' - 9"; MH/2=0' - 9"; MOTOR_BASE=1' - 6"; MOTOR_HEIGHT=1' - 6"; N=3' - 11 1/8"; P=0' - 1"; Type Comments=Centrifugal Plenum Fan Side Mount Arrangement 3S Class 2
- 490_PLC_CLASS_2_3S: -(H-.125")=-0' - 6 7/16"; -F=-4' - 2 11/16"; -F/2=-2' - 1 11/32"; -H+.375"=-0' - 6 3/16"; A=5' - 10"; A/2=2' - 11"; B=5' - 3"; B/2=2' - 7 1/2"; C=2' - 11"; C*.2=0' - 10 1/2"; C*.66=1' - 11 3/32"; C-M=2' - 8 5/16"; C/2=1' - 5 1/2"; D=2' - 7 1/2"; E=2' - 6 1/2"; F=4' - 2 11/16"; F-H-H=3' - 1 9/16"; G=3' - 5 7/8"; H=0' - 6 9/16"; H-.125"=0' - 6 7/16"; J=0' - 7 11/16"; K=4' - 8 13/16"; K-F=0' - 6 1/8"; L=0' - 1 1/16"; L/2=0' - 0 17/32"; M=0' - 2 11/16"; M*2=0' - 5 3/8"; M/2=0' - 1 11/32"; MB/2=0' - 9"; MH/2=0' - 9"; MOTOR_BASE=1' - 6"; MOTOR_HEIGHT=1' - 6"; N=4' - 2 3/8"; P=0' - 1"; Type Comments=Centrifugal Plenum Fan Side Mount Arrangement 3S Class 2
- 540_PLC_CLASS_2_3S: -(H-.125")=-0' - 6 7/16"; -F=-4' - 6 3/8"; -F/2=-2' - 3 3/16"; -H+.375"=-0' - 6 3/16"; A=6' - 3"; A/2=3' - 1 1/2"; B=5' - 9"; B/2=2' - 10 1/2"; C=3' - 2 5/8"; C*.2=0' - 11 19/32"; C*.66=2' - 1 1/2"; C-M=2' - 11 11/16"; C/2=1' - 7 5/16"; D=2' - 10 1/2"; E=2' - 9 1/2"; F=4' - 6 3/8"; F-H-H=3' - 5 1/4"; G=3' - 9 1/2"; H=0' - 6 9/16"; H-.125"=0' - 6 7/16"; J=0' - 7 3/4"; K=5' - 1"; K-F=0' - 6 5/8"; L=0' - 1 1/16"; L/2=0' - 0 17/32"; M=0' - 2 15/16"; M*2=0' - 5 7/8"; M/2=0' - 1 15/32"; MB/2=0' - 9"; MH/2=0' - 9"; MOTOR_BASE=1' - 6"; MOTOR_HEIGHT=1' - 6"; N=4' - 6 1/4"; P=0' - 1 1/4"; Type Comments=Centrifugal Plenum Fan Side Mount Arrangement 3S Class 2
- 600_PLC_CLASS_2_3S: -(H-.125")=-0' - 7"; -F=-4' - 10 1/4"; -F/2=-2' - 5 1/8"; -H+.375"=-0' - 6 3/4"; A=6' - 10"; A/2=3' - 5"; B=6' - 3"; B/2=3' - 1 1/2"; C=3' - 6 7/8"; C*.2=1' - 0 7/8"; C*.66=2' - 4 5/16"; C-M=3' - 3 7/16"; C/2=1' - 9 7/16"; D=3' - 1 1/2"; E=3' - 0 1/2"; F=4' - 10 1/4"; F-H-H=3' - 8"; G=4' - 1 7/8"; H=0' - 7 1/8"; H-.125"=0' - 7"; J=0' - 8 1/4"; K=5' - 6 5/8"; K-F=0' - 8 3/8"; L=0' - 1 1/16"; L/2=0' - 0 17/32"; M=0' - 3 7/16"; M*2=0' - 6 7/8"; M/2=0' - 1 23/32"; MB/2=0' - 10"; MH/2=0' - 10 3/4"; MOTOR_BASE=1' - 8"; MOTOR_HEIGHT=1' - 9 1/2"; N=4' - 9 7/8"; P=0' - 1 1/4"; Type Comments=Centrifugal Plenum Fan Side Mount Arrangement 3S Class 2
- 660_PLC_CLASS_2_3S: -(H-.125")=-0' - 8"; -F=-5' - 4 11/16"; -F/2=-2' - 8 11/32"; -H+.375"=-0' - 7 3/4"; A=7' - 6"; A/2=3' - 9"; B=6' - 10"; B/2=3' - 5"; C=3' - 11 1/4"; C*.2=1' - 2 3/16"; C*.66=2' - 7 3/16"; C-M=3' - 7 13/16"; C/2=1' - 11 5/8"; D=3' - 5"; E=3' - 3 11/16"; F=5' - 4 11/16"; F-H-H=4' - 0 7/16"; G=4' - 6 5/16"; H=0' - 8 1/8"; H-.125"=0' - 8"; J=0' - 9 1/4"; K=6' - 0 13/16"; K-F=0' - 8 1/8"; L=0' - 1 1/16"; L/2=0' - 0 17/32"; M=0' - 3 7/16"; M*2=0' - 6 7/8"; M/2=0' - 1 23/32"; MB/2=0' - 11"; MH/2=0' - 11 3/4"; MOTOR_BASE=1' - 10"; MOTOR_HEIGHT=1' - 11 1/2"; N=5' - 2 7/8"; P=0' - 1 1/2"; Type Comments=Centrifugal Plenum Fan Side Mount Arrangement 3S Class 2
- 730_PLC_CLASS_2_3S: -(H-.125")=-0' - 8"; -F=-5' - 9 3/4"; -F/2=-2' - 10 7/8"; -H+.375"=-0' - 7 3/4"; A=7' - 8"; A/2=3' - 10"; B=7' - 8"; B/2=3' - 10"; C=4' - 4 1/4"; C*.2=1' - 3 11/16"; C*.66=2' - 10 1/2"; C-M=4' - 0 13/16"; C/2=2' - 2 1/8"; D=3' - 10"; E=3' - 8 11/16"; F=5' - 9 3/4"; F-H-H=4' - 5 1/2"; G=4' - 11 3/8"; H=0' - 8 1/8"; H-.125"=0' - 8"; J=0' - 9 1/4"; K=6' - 6 7/8"; K-F=0' - 9 1/8"; L=0' - 1 1/16"; L/2=0' - 0 17/32"; M=0' - 3 7/16"; M*2=0' - 6 7/8"; M/2=0' - 1 23/32"; MB/2=0' - 11"; MH/2=0' - 11 3/4"; MOTOR_BASE=1' - 10"; MOTOR_HEIGHT=1' - 11 1/2"; N=5' - 8 1/2"; P=0' - 1 1/2"; Type Comments=Centrifugal Plenum Fan Side Mount Arrangement 3S Class 2

## geometry (parser evidence)
native form markers: Sweep x1
no freeform markers — native parametric forms only
